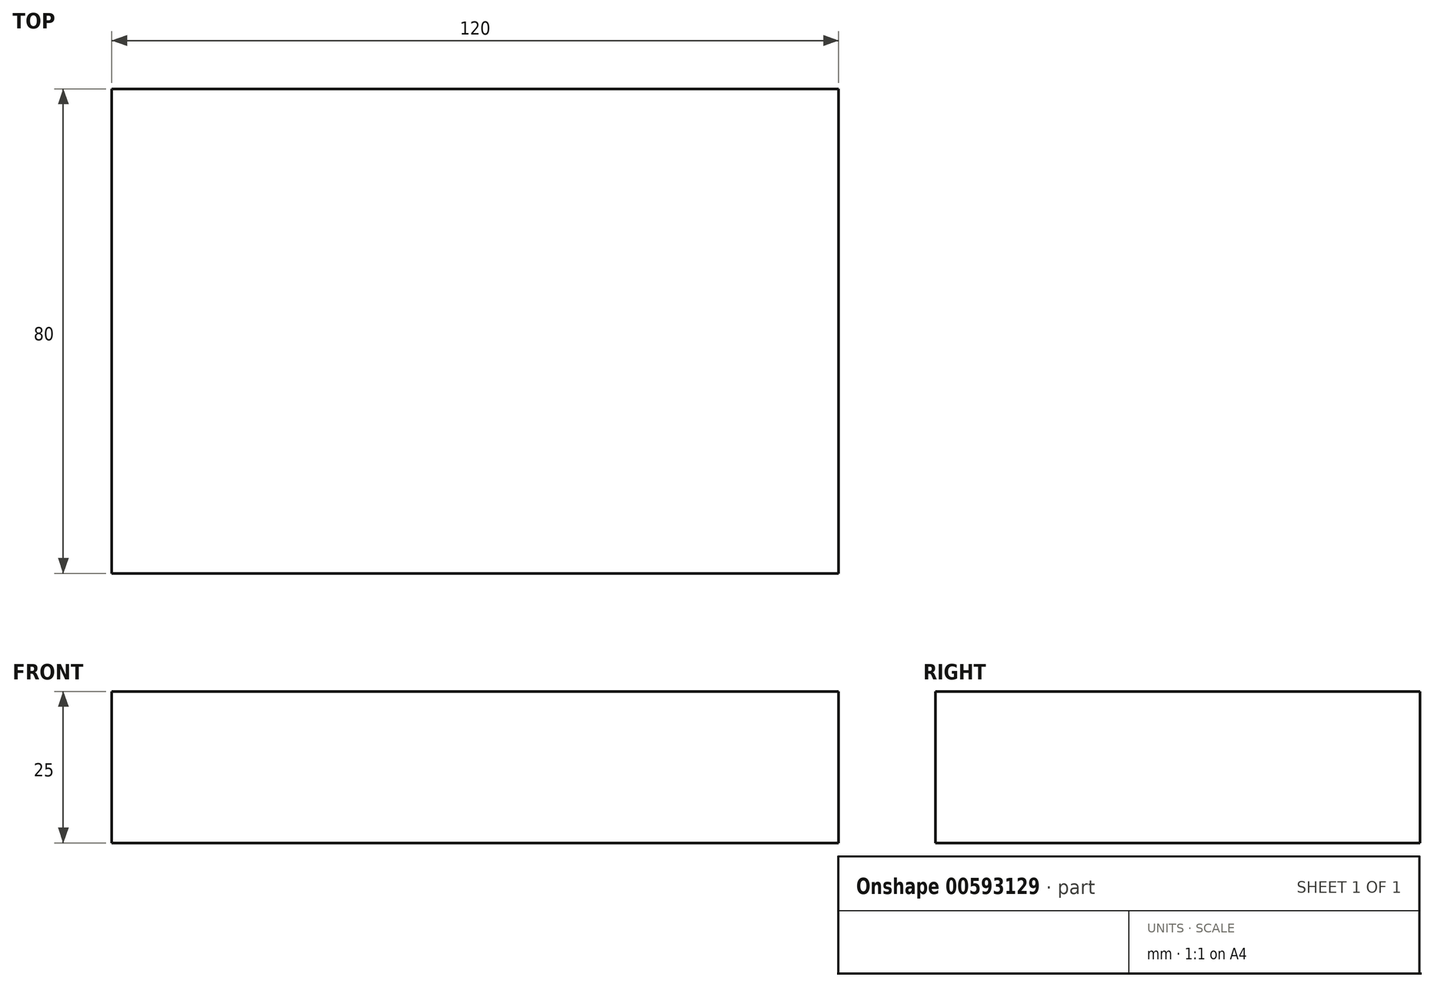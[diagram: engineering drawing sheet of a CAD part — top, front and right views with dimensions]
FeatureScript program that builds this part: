
annotation { "Feature Type Name" : "Feature", "Feature Type Description" : "" }
export const myFeature = defineFeature(function(context is Context, id is Id, definition is map)
    precondition{}
    {
        {
            var Q0;
            Q0=qCreatedBy(makeId("Top.planeOp"),FACE);
            var sketch = newSketch(context, id + "F0", { "sketchPlane" : qUnion([Q0])});
            skLineSegment(sketch, "E0.bottom", {"start": v(60, 40) * mm, "end": v(-60, 40) * mm});
            skLineSegment(sketch, "E0.top", {"start": v(60, -40) * mm, "end": v(-60, -40) * mm});
            skLineSegment(sketch, "E0.left", {"start": v(60, 40) * mm, "end": v(60, -40) * mm});
            skLineSegment(sketch, "E0.right", {"start": v(-60, 40) * mm, "end": v(-60, -40) * mm});
            skPoint(sketch, "E0.middle", {"position": v(0, 0) * mm});
            skSolve(sketch);
        }
        {
            var Q0;
            Q0 = qSketchRegion(id + "F0", true);
            extrude(context, id + "F1", {"entities" : qUnion([Q0]), "depth" : 25 * mm, "offsetDistance" : 25 * mm});
        }
    });
